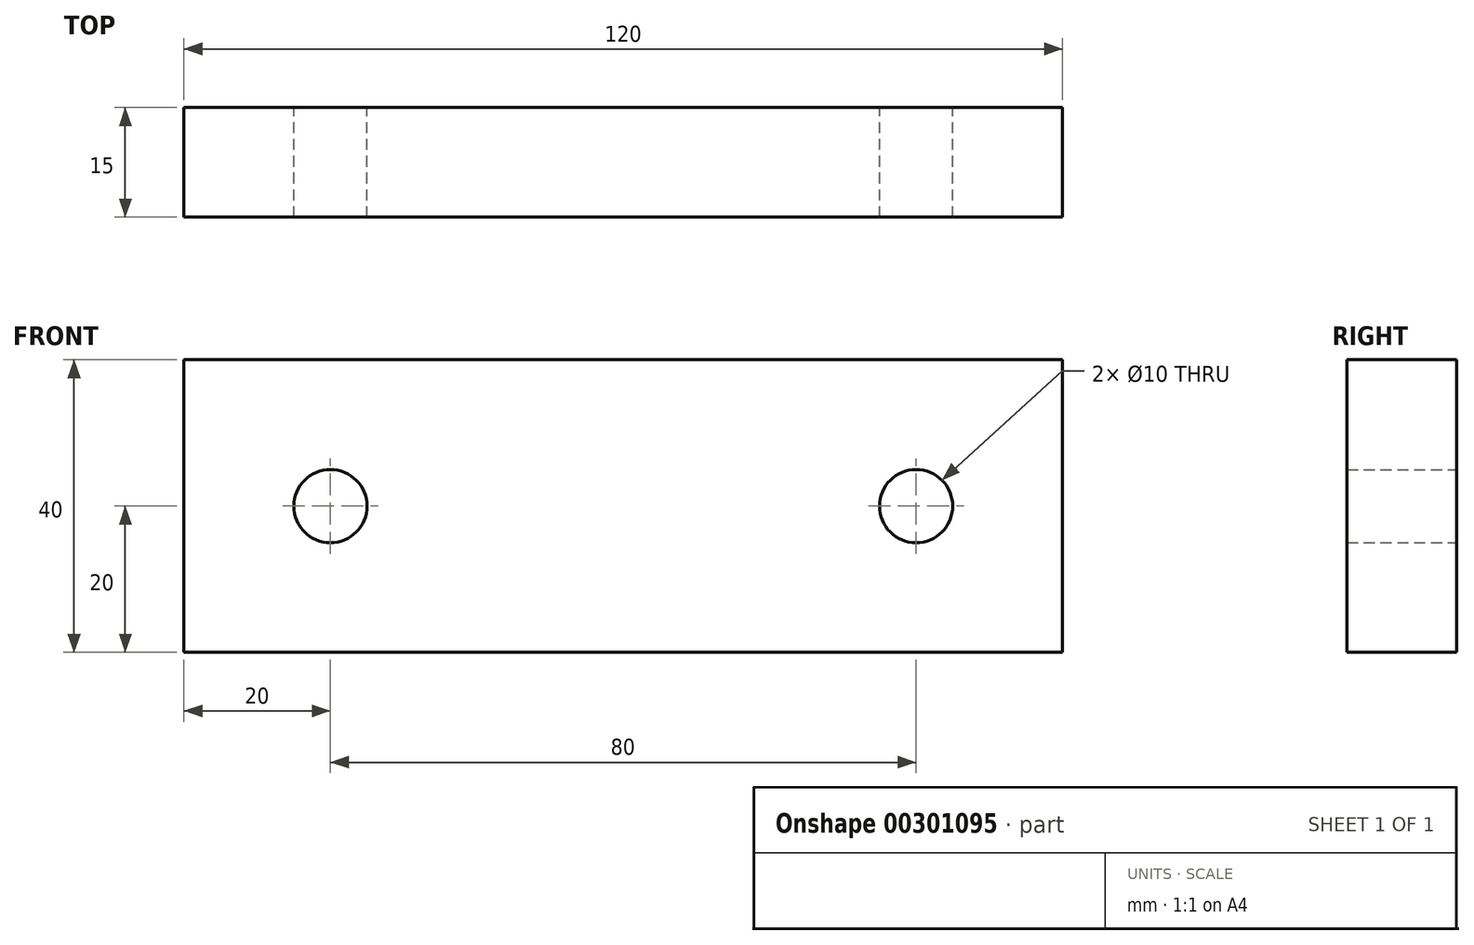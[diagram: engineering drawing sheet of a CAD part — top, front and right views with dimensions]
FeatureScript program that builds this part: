
annotation { "Feature Type Name" : "Feature", "Feature Type Description" : "" }
export const myFeature = defineFeature(function(context is Context, id is Id, definition is map)
    precondition{}
    {
        {
            var Q0;
            Q0=qCreatedBy(makeId("Front.planeOp"),FACE);
            var sketch = newSketch(context, id + "F0", { "sketchPlane" : qUnion([Q0])});
            skLineSegment(sketch, "E0.bottom", {"start": v(0, 0) * mm, "end": v(120, 0) * mm});
            skLineSegment(sketch, "E0.top", {"start": v(0, 40) * mm, "end": v(120, 40) * mm});
            skLineSegment(sketch, "E0.left", {"start": v(0, 0) * mm, "end": v(0, 40) * mm});
            skLineSegment(sketch, "E0.right", {"start": v(120, 0) * mm, "end": v(120, 40) * mm});
            skCircle(sketch, "E1", {"center": v(20, 20) * mm, "radius": 5 * mm});
            skCircle(sketch, "E2", {"center": v(100, 20) * mm, "radius": 5 * mm});
            skSolve(sketch);
        }
        {
            var Q0;
            Q0 = qSketchRegion(id + "F0", true);
            extrude(context, id + "F1", {"entities" : qUnion([Q0]), "depth" : 15 * mm});
        }
        {
            var Q0;
            Q0 = qSketchRegion(id + "F0", true);
            extrude(context, id + "F2", {"entities" : qUnion([Q0]), "operationType" : NewBodyOperationType.ADD, "depth" : 15 * mm});
        }
    });
